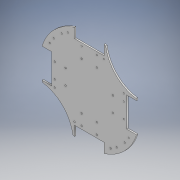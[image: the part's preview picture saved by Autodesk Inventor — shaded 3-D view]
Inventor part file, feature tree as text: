
AUTODESK INVENTOR PART (.ipt)
format: ipt  version: 2020 (Build 240168000, 168)  size: 216,576 bytes
history: native  units: mm
features: extrude x2, sketch x2, other x1
ambient origin geometry x8: Origin, YZ Plane, XZ Plane, XY Plane, X Axis, Y Axis, Z Axis, Center Point
bodies: Body1 (feature_tree)
feature tree (5):
  other  "Твердое тело1"
  extrude  "Выдавливание1"  Depth=215.0mm
  extrude  "Выдавливание2"  Depth=208.0mm
  sketch  "Эскиз2"
  sketch  "Эскиз3"
